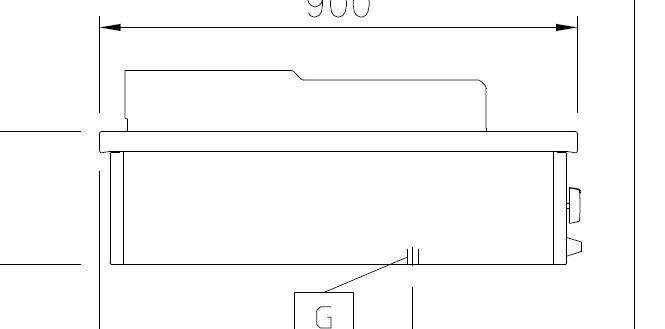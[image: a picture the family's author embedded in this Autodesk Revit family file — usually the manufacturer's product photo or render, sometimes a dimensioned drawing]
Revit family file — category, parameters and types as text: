
# Revit family: QF_ELECTROLUXPROFESSIONAL_593300_MCDAAADOVO
name_source: partatom
category: Specialty Equipment
revit_build: Autodesk Revit 2018 (Build: 20190510_1515(x64)
units: mm (PartAtom-declared; Revit-internal decimal feet)

## family parameters
Always vertical = Yes
Cut with Voids When Loaded = No
Part Type = Normal
Room Calculation Point = No
Round Connector Dimension = Use Diameter
Shared = No
Work Plane-Based = No

## types (1)
- Standard
    Accessory = Yes
    Cold Water Size = 0"
    Compressed Air Pressure = 0.00 psi
    Compressed Air Size = 0"
    Compressed Air Volume = 0 GPM
    Condensate Return Size = 0"
    Cycle = 0 Hz
    Depth Actual = 900 mm  [stored 2.95276 ft]
    Description = GAS CHARGRILL,TOWNGAS,1S,400X900X250H
    Direct Waste Size = 0"
    Gas Input Pressure = 0.8
    Gas KW = 9.5
    Gas Size = 1"
    HP = 0 HP
    Height Actual = 250 mm  [stored 0.82021 ft]
    Hot Water Size = 0"
    Item Number = 593300
    Length Actual = 400 mm  [stored 1.31234 ft]
    Manufacturer = Electrolux Professional
    Model = MCDAAADOVO
    Phase = 0
    Refrigerant Compressor Remote = Yes
    Refrigeration Liquid Line Size = 0 mm  [stored 0 ft]
    Refrigeration Suction Line Size = 0 mm  [stored 0 ft]
    Steam Pounds per Hour = 0
    Steam Supply Maximum Pressure = 0.00 psi
    Steam Supply Minimum Pressure = 0.00 psi
    Steam Supply Size = 0"
    URL = http://professional.electrolux.com
    URL Manufacturer = http://professional.electrolux.com
    Volts = 0 V
    Watts = 0 W
    Weight = 65.00 kg

note: source unit labels omitted for Gas Input Pressure — the stored unit's dimension contradicts the parameter name (converter mislabeling)

note: [stored X ft] marks values corroborated as IEEE doubles in the binary element streams (Revit-internal decimal feet)

## geometry (parser evidence)
native form markers: Blend x20, Sweep x14
no freeform markers — native parametric forms only
